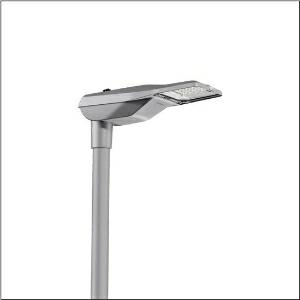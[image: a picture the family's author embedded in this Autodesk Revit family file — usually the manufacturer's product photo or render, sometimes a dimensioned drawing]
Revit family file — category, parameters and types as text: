
# Revit family: streetlight_sl_21_iq_micro___p0_5a_5xe1v31v08db_2d7c
name_source: partatom
category: Lighting Fixtures
units: mm (PartAtom-declared; Revit-internal decimal feet)

## family parameters
Cut with Voids When Loaded = No
Host = Face
Light Source = No
Part Type = Normal
Room Calculation Point = No
Round Connector Dimension = Use Diameter
Shared = No

## types (1)
- --- (1 x LED, 5030 lm, 39.1 W, 3000K)
    Apparent Load = 39 VA
    CIE Flux Codes = 37 73 96 100 100
    Color Rendering = 70
    Color Temperature = 3000K
    Default Elevation = 1800 mm
    Description = Streetlight SL 21 iQ micro, mast luminaire, primary light control with lens, of PMMA, primary optical cover: cover, of toughened safety glass, transparent, light distribution: P0.5a, light emission: direct distribution, primary light characteristic: asymmetric, installation type: post-top, side-entry, LED, High Power LED, rated luminous flux: 5.030lm, luminous efficacy: 129lm/W, light colour: 730, colour temperature: 3000K, control gear: iQ-Street Remote, D4i with power reduction, control: pre-setting: logarithmic dimming characteristic, Street-Remote, Auto-Match, Temp-Guard, Lumen-Switch, Night-Set, Smart-Wire, Light-Fading, Desk-Remote (wireless, voltage-free reading and setting of iQ features in the workshop via application-optimized NFC function/RFID function), optimised constant luminous flux control (CLO 2.0), mains connection: 220..240V, AC, 50/60Hz, start of lifetime: 39W, end of service life: 41W, reduction: 17W, luminaire housing, of diecast aluminium, powder-coated, SITECO metallic grey (DB 702S), corrosivity category C5 high according to DIN EN ISO 12944, please order mast flange separately, inclination adjustable: 0°, 5°, 10°, 15°, sealing non-destructively replaceable, multi-level sealing system, length: 528mm, width: 235mm, height: 110mm, mast flange for spigot size: 42mm (side-entry): 5XC10008XM4, 60/48mm (side-entry/post-top): 5XC10108XM2, 76/60mm (side-entry/post-top): 5XC10108XM1, mounting height: 4..8m, Smart Interface above, protection rating (complete): IP66, insulation class (complete): insulation class II (safety insulation), certification: CE, ENEC, ENEC+, VDE, impact resistance: IK10, permissible operating ambient temperature for outdoor applications: -40..+50°C, standard-compliant lighting for roads and squares, packaging unit: 1 piece

Light Distribution: P0.5a
    Height = 110 mm
    Lamp = 1 x LED
    Lamp Light Flux = 5030 lm
    Lamp Power = 39.1 W
    Lamp count = 1
    Length = 528 mm
    Luminous efficacy = 129 lm/W
    Manufacturer = Siteco
    ModVariant = No
    Model = 5XE1V31V08DB
    Number of Poles = 1
    OnlyDefault = Yes
    Power Factor = 1
    Product Name = Streetlight SL 21 iQ micro | P0.5a
    Product group = mast luminaire | pylon top
    ProductGroupID = 6100
    Protection Class = Protection class II
    Protection Degree = IP 66
    RLX_Detail_Level = 1
    RLX_Emergency_Light_Flux = 0 lm
    RLX_Emergency_Type = 0
    RLX_Emergency_Type_DB = No
    RlxData = <blob elided: 98781 chars, md5=2eef5604>
    Socket = socket
    Standby Power = 0 W
    System Light Flux = 5030 lm
    System Power = 39 W
    Type Comments = factory setting: luminous flux: 100 % | dim-lin: 254 | 765 mA
    Type Image = l_1277292.jpg
    URL = http://relux.com
    VarID = @adj_078569
    Voltage = 0 V
    Weight = 0.00 kg
    Width = 235 mm

## geometry (parser evidence)
native form markers: Blend x4, Sweep x12
no freeform markers — native parametric forms only
